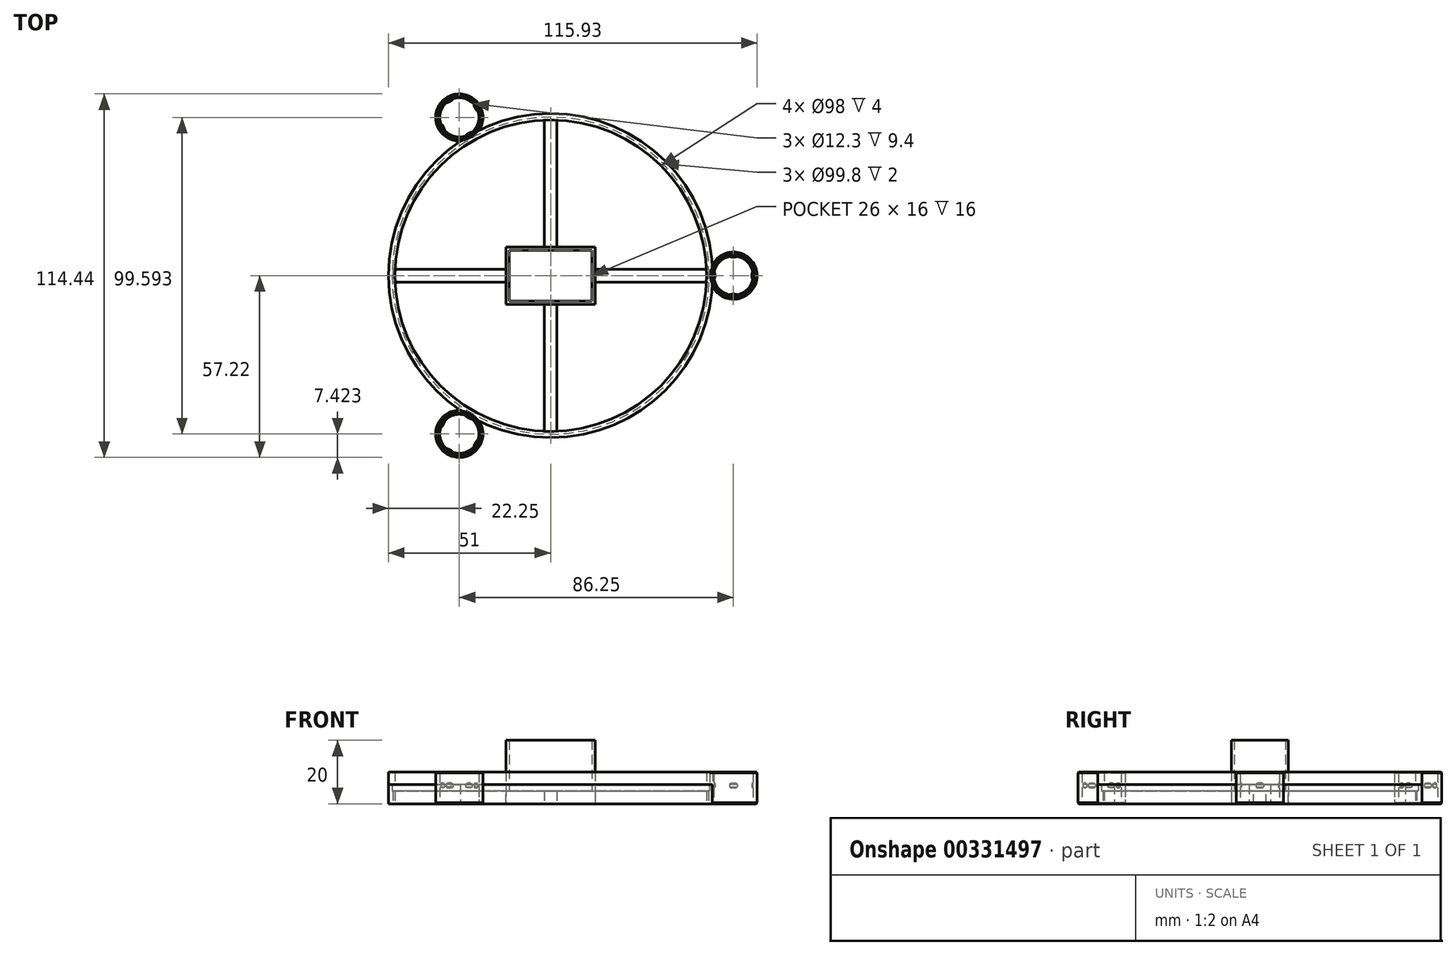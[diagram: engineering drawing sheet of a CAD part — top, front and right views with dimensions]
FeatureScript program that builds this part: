
annotation { "Feature Type Name" : "Feature", "Feature Type Description" : "" }
export const myFeature = defineFeature(function(context is Context, id is Id, definition is map)
    precondition{}
    {
        {
            var Q0;
            Q0=qCreatedBy(makeId("Top.planeOp"),FACE);
            var sketch = newSketch(context, id + "F0", { "sketchPlane" : qUnion([Q0])});
            skCircle(sketch, "E0", {"center": v(0, 0) * mm, "radius": 6.15 * mm});
            skArc(sketch, "E1", {"start": v(1.2, -6.03) * mm, "mid": v(0, -5.78) * mm, "end": v(-1.2, -6.03) * mm});
            skArc(sketch, "E2.1.0", {"start": v(6.03, 1.2) * mm, "mid": v(5.78, 0) * mm, "end": v(6.03, -1.2) * mm});
            skArc(sketch, "E2.2.0", {"start": v(-1.2, 6.03) * mm, "mid": v(0, 5.78) * mm, "end": v(1.2, 6.03) * mm});
            skArc(sketch, "E2.3.0", {"start": v(-6.03, -1.2) * mm, "mid": v(-5.78, 0) * mm, "end": v(-6.03, 1.2) * mm});
            skCircle(sketch, "E3.0", {"center": v(0, 0) * mm, "radius": 4.68 * mm});
            skCircle(sketch, "E4", {"center": v(0, 0) * mm, "radius": 7.42 * mm});
            skLineSegment(sketch, "E5", {"start": v(0, -4.68) * mm, "end": v(0, -6.15) * mm, "construction": true});
            skPoint(sketch, "E5.endSnap0", {"position": v(0, -5.41) * mm});
            skPoint(sketch, "E6", {"position": v(0, -5.78) * mm});
            skSolve(sketch);
        }
        {
            assignVariable(context, id + "F1", {"name" : "BumpStart", "anyValue" : 5});
        }
        {
            assignVariable(context, id + "F2", {"name" : "BumpEnd", "anyValue" : 6.5});
        }
        {
            assignVariable(context, id + "F3", {"name" : "Height", "anyValue" : 10});
        }
        {
            var Q0;
            Q0=makeQuery(id+"F0.imprint","IMPRINT",FACE,{"disambiguationData":[TD([[makeQuery(id+"F0.imprint","IMPRINT",EDGE,{"derivedFrom":sQuery(id+"F0.wireOp",EDGE,"E4")}),1.0]])]});
            extrude(context, id + "F4", {"entities" : qUnion([Q0]), "depth" : (getVariable(context, 'Height')) * mm});
        }
        {
            var Q0;
            {var subQ0=sQuery(id+"F0.wireOp",EDGE,"E2.3.0");Q0=makeQuery(id+"F0.imprint","IMPRINT",FACE,{"disambiguationData":[TD([[makeQuery(id+"F0.imprint","IMPRINT",EDGE,{"derivedFrom":subQ0}),1.0]])]});}
            var Q1;
            {var subQ0=sQuery(id+"F0.wireOp",EDGE,"E1");Q1=makeQuery(id+"F0.imprint","IMPRINT",FACE,{"disambiguationData":[TD([[makeQuery(id+"F0.imprint","IMPRINT",EDGE,{"derivedFrom":subQ0}),1.0]])]});}
            var Q2;
            {var subQ0=sQuery(id+"F0.wireOp",EDGE,"E2.1.0");Q2=makeQuery(id+"F0.imprint","IMPRINT",FACE,{"disambiguationData":[TD([[makeQuery(id+"F0.imprint","IMPRINT",EDGE,{"derivedFrom":subQ0}),1.0]])]});}
            var Q3;
            {var subQ0=sQuery(id+"F0.wireOp",EDGE,"E2.2.0");Q3=makeQuery(id+"F0.imprint","IMPRINT",FACE,{"disambiguationData":[TD([[makeQuery(id+"F0.imprint","IMPRINT",EDGE,{"derivedFrom":subQ0}),1.0]])]});}
            extrude(context, id + "F5", {"entities" : qUnion([Q0, Q1, Q2, Q3]), "operationType" : NewBodyOperationType.ADD, "depth" : (getVariable(context, 'BumpEnd')) * mm, "hasSecondDirection" : true, "secondDirectionOppositeDirection" : false, "secondDirectionDepth" : (getVariable(context, 'BumpStart')) * mm});
        }
        {
            var Q0;
            Q0=makeQuery(id+"F5.opExtrude","CAP_EDGE",EDGE,{"disambiguationData":[OSD([sQuery(id+"F0.wireOp",EDGE,"E2.3.0")])],"isStart":true});
            var Q1;
            Q1=makeQuery(id+"F5.opExtrude","CAP_EDGE",EDGE,{"disambiguationData":[OSD([sQuery(id+"F0.wireOp",EDGE,"E2.3.0")])],"isStart":false});
            var Q2;
            Q2=makeQuery(id+"F5.opExtrude","CAP_EDGE",EDGE,{"disambiguationData":[OSD([sQuery(id+"F0.wireOp",EDGE,"E1")])],"isStart":true});
            var Q3;
            Q3=makeQuery(id+"F5.opExtrude","CAP_EDGE",EDGE,{"disambiguationData":[OSD([sQuery(id+"F0.wireOp",EDGE,"E1")])],"isStart":false});
            var Q4;
            Q4=makeQuery(id+"F5.opExtrude","CAP_EDGE",EDGE,{"disambiguationData":[OSD([sQuery(id+"F0.wireOp",EDGE,"E2.2.0")])],"isStart":true});
            var Q5;
            Q5=makeQuery(id+"F5.opExtrude","CAP_EDGE",EDGE,{"disambiguationData":[OSD([sQuery(id+"F0.wireOp",EDGE,"E2.2.0")])],"isStart":false});
            var Q6;
            Q6=makeQuery(id+"F5.opExtrude","CAP_EDGE",EDGE,{"disambiguationData":[OSD([sQuery(id+"F0.wireOp",EDGE,"E2.1.0")])],"isStart":true});
            var Q7;
            Q7=makeQuery(id+"F5.opExtrude","CAP_EDGE",EDGE,{"disambiguationData":[OSD([sQuery(id+"F0.wireOp",EDGE,"E2.1.0")])],"isStart":false});
            chamfer(context, id + "F6", {"entities" : qUnion([Q0, Q1, Q2, Q3, Q4, Q5, Q6, Q7]), "width" : .3 * mm, "tangentPropagation" : true});
        }
        {
            var Q0;
            Q0=makeQuery(id+"F4.opExtrude","CAP_FACE",FACE,{"disambiguationData":[OSD([sQuery(id+"F0.wireOp",EDGE,"E0"),sQuery(id+"F0.wireOp",EDGE,"E4")])],"isStart":true});
            var Q1;
            {var subQ0=sQuery(id+"F0.wireOp",EDGE,"E3.0");var subQ1=sQuery(id+"F0.wireOp",EDGE,"E0");Q1=makeQuery(id+"F6UwThijnyDj1M6_1.boolean.opBoolean","MERGE",FACE,{"derivedFrom":[makeQuery(id+"FqQ50qO7LfDwovo_1.boolean.opBoolean","MERGE",FACE,{"derivedFrom":[makeQuery(id+"F4.opExtrude","CAP_FACE",FACE,{"disambiguationData":[OSD([subQ1,sQuery(id+"F0.wireOp",EDGE,"E4")])],"isStart":false}),makeQuery(id+"FqQ50qO7LfDwovo_1.opExtrude","CAP_FACE",FACE,{"disambiguationData":[OSD([subQ1,subQ0])],"isStart":false})]}),makeQuery(id+"F6UwThijnyDj1M6_1.opExtrude","CAP_FACE",FACE,{"disambiguationData":[OSD([subQ0])],"isStart":false})]});}
            chamfer(context, id + "F7", {"entities" : qUnion([Q0, Q1]), "width" : 0.3 * mm, "tangentPropagation" : true});
        }
        {
            var Q0;
            Q0=qCreatedBy(makeId("Top.planeOp"),FACE);
            var sketch = newSketch(context, id + "F8", { "sketchPlane" : qUnion([Q0])});
            skCircle(sketch, "E7", {"center": v(-57.5, 0) * mm, "radius": 51 * mm});
            skCircle(sketch, "E8", {"center": v(-57.5, 0) * mm, "radius": 49 * mm});
            skSolve(sketch);
        }
        {
            var Q0;
            Q0 = qSketchRegion(id + "F8", true);
            extrude(context, id + "F9", {"entities" : qUnion([Q0]), "operationType" : NewBodyOperationType.ADD, "depth" : 4 * mm});
        }
        {
            var Q0;
            Q0=makeQuery(id+"F9.opExtrude","CAP_FACE",FACE,{"disambiguationData":[OSD([sQuery(id+"F8.wireOp",EDGE,"E7"),sQuery(id+"F8.wireOp",EDGE,"E8")])],"isStart":false});
            var sketch = newSketch(context, id + "F10", { "sketchPlane" : qUnion([Q0])});
            skCircle(sketch, "E9", {"center": v(-57.5, 0) * mm, "radius": 51 * mm});
            skCircle(sketch, "E10", {"center": v(-57.5, 0) * mm, "radius": 49.9 * mm});
            skSolve(sketch);
        }
        {
            var Q0;
            Q0 = qSketchRegion(id + "F10", true);
            extrude(context, id + "F11", {"entities" : qUnion([Q0]), "operationType" : NewBodyOperationType.ADD, "depth" : 2 * mm});
        }
        {
            var Q0;
            Q0=makeQuery(id+"F11.opExtrude","CAP_FACE",FACE,{"disambiguationData":[OSD([sQuery(id+"F10.wireOp",EDGE,"E9"),sQuery(id+"F10.wireOp",EDGE,"E10")])],"isStart":false});
            var sketch = newSketch(context, id + "F12", { "sketchPlane" : qUnion([Q0])});
            skCircle(sketch, "E11", {"center": v(-57.5, 0) * mm, "radius": 51 * mm});
            skCircle(sketch, "E12", {"center": v(-57.5, 0) * mm, "radius": 49 * mm});
            skSolve(sketch);
        }
        {
            var Q0;
            Q0=qCreatedBy(makeId("Front.planeOp"),FACE);
            var sketch = newSketch(context, id + "F13", { "sketchPlane" : qUnion([Q0])});
            skLineSegment(sketch, "E13", {"start": v(-57.5, 0) * mm, "end": v(-57.5, 29.43) * mm, "construction": true});
            skSolve(sketch);
        }
        {
            var Q0;
            Q0=makeQuery(id+"F4.opExtrude","SWEPT_BODY",BODY,{"disambiguationData":[OSD([sQuery(id+"F0.wireOp",EDGE,"E0"),sQuery(id+"F0.wireOp",EDGE,"E4")])]});
            var Q1;
            Q1=sQuery(id+"F13.wireOp",EDGE,"E13");
            circularPattern(context, id + "F14", {"entities" : qUnion([Q0]), "axis" : qUnion([Q1]), "angle" : 360 * degree, "instanceCount" : 3, "equalSpace" : true});
        }
        {
            var Q0;
            {var subQ1=sQuery(id+"F10.wireOp",EDGE,"E10");Q0=makeQuery(id+"F12.imprint","IMPRINT",FACE,{"disambiguationData":[TD([[makeQuery(id+"F12.imprint","IMPRINT",EDGE,{"derivedFrom":makeQuery(id+"F11.opExtrude","CAP_EDGE",EDGE,{"disambiguationData":[OSD([subQ1])],"isStart":false})}),-1.0]])]});}
            var sketch = newSketch(context, id + "F15", { "sketchPlane" : qUnion([Q0])});
            skCircle(sketch, "E14", {"center": v(-57.5, 0) * mm, "radius": 51 * mm});
            skCircle(sketch, "E15", {"center": v(-57.5, 0) * mm, "radius": 49 * mm});
            skSolve(sketch);
        }
        {
            var Q0;
            Q0 = qSketchRegion(id + "F15", true);
            extrude(context, id + "F16", {"entities" : qUnion([Q0]), "depth" : 4 * mm});
        }
        {
            var Q0;
            Q0=qCreatedBy(makeId("Top.planeOp"),FACE);
            var sketch = newSketch(context, id + "F17", { "sketchPlane" : qUnion([Q0])});
            skLineSegment(sketch, "E16.bottom", {"start": v(-70.5, 8) * mm, "end": v(-44.5, 8) * mm});
            skLineSegment(sketch, "E16.top", {"start": v(-70.5, -8) * mm, "end": v(-44.5, -8) * mm});
            skLineSegment(sketch, "E16.left", {"start": v(-70.5, 8) * mm, "end": v(-70.5, -8) * mm});
            skLineSegment(sketch, "E16.right", {"start": v(-44.5, 8) * mm, "end": v(-44.5, -8) * mm});
            skLineSegment(sketch, "E17", {"start": v(-57.5, 0) * mm, "end": v(-57.5, 35.38) * mm, "construction": true});
            skLineSegment(sketch, "E18.bottom", {"start": v(-44.5, 2) * mm, "end": v(-7.81, 2) * mm});
            skLineSegment(sketch, "E18.top", {"start": v(-44.5, -2) * mm, "end": v(-7.81, -2) * mm});
            skLineSegment(sketch, "E18.left", {"start": v(-44.5, 2) * mm, "end": v(-44.5, -2) * mm});
            skLineSegment(sketch, "E18.right", {"start": v(-7.81, 2) * mm, "end": v(-7.81, -2) * mm});
            skLineSegment(sketch, "E19.MirrorCS", {"start": v(-70.5, 2) * mm, "end": v(-107.19, 2) * mm});
            skLineSegment(sketch, "E20.MirrorCS", {"start": v(-70.5, -2) * mm, "end": v(-107.19, -2) * mm});
            skLineSegment(sketch, "E21.MirrorCS", {"start": v(-107.19, 2) * mm, "end": v(-107.19, -2) * mm});
            skLineSegment(sketch, "E22.bottom", {"start": v(-59.5, 49.28) * mm, "end": v(-55.5, 49.28) * mm});
            skLineSegment(sketch, "E22.top", {"start": v(-59.5, 8) * mm, "end": v(-55.5, 8) * mm});
            skLineSegment(sketch, "E22.left", {"start": v(-59.5, 49.28) * mm, "end": v(-59.5, 8) * mm});
            skLineSegment(sketch, "E22.right", {"start": v(-55.5, 49.28) * mm, "end": v(-55.5, 8) * mm});
            skLineSegment(sketch, "E23.MirrorCS", {"start": v(-55.5, -49.28) * mm, "end": v(-55.5, -8) * mm});
            skLineSegment(sketch, "E24.MirrorCS", {"start": v(-59.5, -49.28) * mm, "end": v(-59.5, -8) * mm});
            skLineSegment(sketch, "E25.MirrorCS", {"start": v(-59.5, -49.28) * mm, "end": v(-55.5, -49.28) * mm});
            skSolve(sketch);
        }
        {
            var Q0;
            Q0 = qSketchRegion(id + "F17", true);
            var Q1;
            Q1=makeQuery(id+"F9.opExtrude","CAP_FACE",FACE,{"disambiguationData":[OSD([sQuery(id+"F8.wireOp",EDGE,"E7"),sQuery(id+"F8.wireOp",EDGE,"E8")])],"isStart":false});
            extrude(context, id + "F18", {"entities" : qUnion([Q0]), "endBound" : BoundingType.UP_TO_SURFACE, "endBoundEntityFace" : qUnion([Q1]), "depth" : 25 * mm});
        }
        {
            var Q0;
            Q0=qCreatedBy(makeId("Top.planeOp"),FACE);
            var sketch = newSketch(context, id + "F19", { "sketchPlane" : qUnion([Q0])});
            skLineSegment(sketch, "E26.bottom", {"start": v(-71.5, 9) * mm, "end": v(-43.5, 9) * mm});
            skLineSegment(sketch, "E26.top", {"start": v(-71.5, -9) * mm, "end": v(-43.5, -9) * mm});
            skLineSegment(sketch, "E26.left", {"start": v(-71.5, 9) * mm, "end": v(-71.5, -9) * mm});
            skLineSegment(sketch, "E26.right", {"start": v(-43.5, 9) * mm, "end": v(-43.5, -9) * mm});
            skLineSegment(sketch, "E27.bottom", {"start": v(-70.5, 8) * mm, "end": v(-44.5, 8) * mm});
            skLineSegment(sketch, "E27.top", {"start": v(-70.5, -8) * mm, "end": v(-44.5, -8) * mm});
            skLineSegment(sketch, "E27.left", {"start": v(-70.5, 8) * mm, "end": v(-70.5, -8) * mm});
            skLineSegment(sketch, "E27.right", {"start": v(-44.5, 8) * mm, "end": v(-44.5, -8) * mm});
            skSolve(sketch);
        }
        {
            var Q0;
            Q0 = qSketchRegion(id + "F19", true);
            extrude(context, id + "F20", {"entities" : qUnion([Q0]), "operationType" : NewBodyOperationType.ADD, "depth" : 20 * mm});
        }
    });
